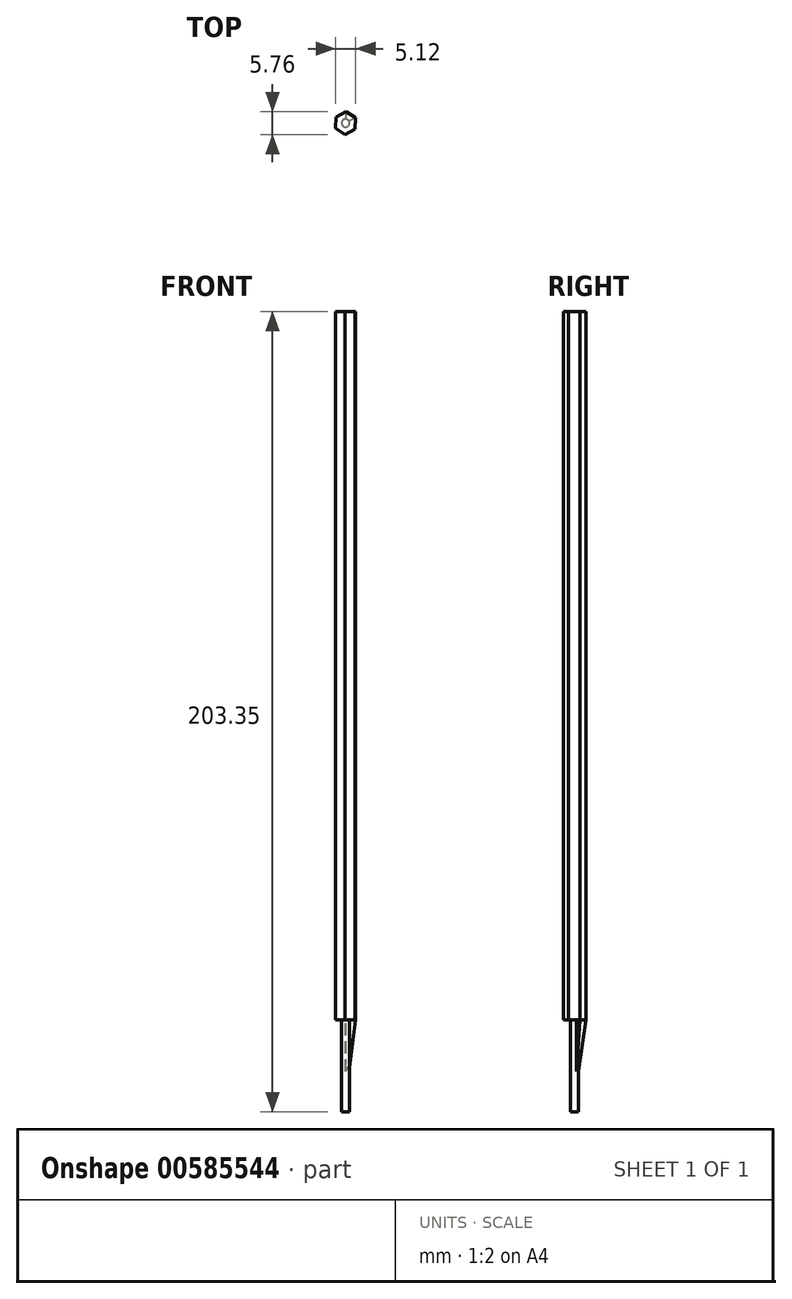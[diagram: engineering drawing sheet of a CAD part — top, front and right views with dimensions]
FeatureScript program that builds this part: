
annotation { "Feature Type Name" : "Feature", "Feature Type Description" : "" }
export const myFeature = defineFeature(function(context is Context, id is Id, definition is map)
    precondition{}
    {
        {
            var Q0;
            Q0=qCreatedBy(makeId("Top.planeOp"),FACE);
            var sketch = newSketch(context, id + "F0", { "sketchPlane" : qUnion([Q0])});
            skCircle(sketch, "E0", {"center": v(0, 0) * mm, "radius": 2.5 * mm});
            skCircle(sketch, "E1.cCircle", {"center": v(0, 0) * mm, "radius": 2.5 * mm, "construction": true});
            skLineSegment(sketch, "E1.0", {"start": v(0.12, 2.88) * mm, "end": v(2.56, 1.34) * mm});
            skLineSegment(sketch, "E1.1", {"start": v(2.56, 1.34) * mm, "end": v(2.44, -1.54) * mm});
            skLineSegment(sketch, "E1.2", {"start": v(2.44, -1.54) * mm, "end": v(-0.12, -2.88) * mm});
            skLineSegment(sketch, "E1.3", {"start": v(-0.12, -2.88) * mm, "end": v(-2.56, -1.34) * mm});
            skLineSegment(sketch, "E1.4", {"start": v(-2.56, -1.34) * mm, "end": v(-2.44, 1.54) * mm});
            skLineSegment(sketch, "E1.5", {"start": v(-2.44, 1.54) * mm, "end": v(0.12, 2.88) * mm});
            skPoint(sketch, "E1.0.midPoint", {"position": v(1.34, 2.11) * mm});
            skCircle(sketch, "E2", {"center": v(0, 0) * mm, "radius": 1 * mm});
            skSolve(sketch);
        }
        {
            var Q0;
            {var subQ0=sQuery(id+"F0.wireOp",EDGE,"E1.4");var subQ1=sQuery(id+"F0.wireOp",EDGE,"E0");var subQ2=makeQuery(id+"F0.imprint","INTERSECT",VERTEX,{"derivedFrom":[subQ1,subQ0]});Q0=makeQuery(id+"F0.imprint","IMPRINT",FACE,{"disambiguationData":[TD([[makeQuery(id+"F0.imprint","IMPRINT",EDGE,{"disambiguationData":[TD([[subQ2,-1.0]])],"derivedFrom":subQ1}),-1.0]])]});}
            var Q1;
            {var subQ0=sQuery(id+"F0.wireOp",EDGE,"E1.3");var subQ1=sQuery(id+"F0.wireOp",EDGE,"E0");var subQ2=makeQuery(id+"F0.imprint","INTERSECT",VERTEX,{"derivedFrom":[subQ1,subQ0]});Q1=makeQuery(id+"F0.imprint","IMPRINT",FACE,{"disambiguationData":[TD([[makeQuery(id+"F0.imprint","IMPRINT",EDGE,{"disambiguationData":[TD([[subQ2,-1.0]])],"derivedFrom":subQ1}),-1.0]])]});}
            var Q2;
            {var subQ0=sQuery(id+"F0.wireOp",EDGE,"E1.5");var subQ1=sQuery(id+"F0.wireOp",EDGE,"E0");var subQ2=makeQuery(id+"F0.imprint","INTERSECT",VERTEX,{"derivedFrom":[subQ1,subQ0]});Q2=makeQuery(id+"F0.imprint","IMPRINT",FACE,{"disambiguationData":[TD([[makeQuery(id+"F0.imprint","IMPRINT",EDGE,{"disambiguationData":[TD([[subQ2,1.0]])],"derivedFrom":subQ1}),-1.0]])]});}
            var Q3;
            {var subQ0=sQuery(id+"F0.wireOp",EDGE,"E1.5");var subQ1=sQuery(id+"F0.wireOp",EDGE,"E0");var subQ2=makeQuery(id+"F0.imprint","INTERSECT",VERTEX,{"derivedFrom":[subQ1,subQ0]});Q3=makeQuery(id+"F0.imprint","IMPRINT",FACE,{"disambiguationData":[TD([[makeQuery(id+"F0.imprint","IMPRINT",EDGE,{"disambiguationData":[TD([[subQ2,-1.0]])],"derivedFrom":subQ1}),-1.0]])]});}
            var Q4;
            {var subQ0=sQuery(id+"F0.wireOp",EDGE,"E1.2");var subQ1=sQuery(id+"F0.wireOp",EDGE,"E0");var subQ2=makeQuery(id+"F0.imprint","INTERSECT",VERTEX,{"derivedFrom":[subQ1,subQ0]});Q4=makeQuery(id+"F0.imprint","IMPRINT",FACE,{"disambiguationData":[TD([[makeQuery(id+"F0.imprint","IMPRINT",EDGE,{"disambiguationData":[TD([[subQ2,-1.0]])],"derivedFrom":subQ1}),-1.0]])]});}
            var Q5;
            {var subQ0=sQuery(id+"F0.wireOp",EDGE,"E1.0");var subQ1=sQuery(id+"F0.wireOp",EDGE,"E0");var subQ2=makeQuery(id+"F0.imprint","INTERSECT",VERTEX,{"derivedFrom":[subQ1,subQ0]});Q5=makeQuery(id+"F0.imprint","IMPRINT",FACE,{"disambiguationData":[TD([[makeQuery(id+"F0.imprint","IMPRINT",EDGE,{"disambiguationData":[TD([[subQ2,1.0]])],"derivedFrom":subQ1}),-1.0]])]});}
            var Q6;
            Q6=makeQuery(id+"F0.imprint","IMPRINT",FACE,{"disambiguationData":[TD([[makeQuery(id+"F0.imprint","IMPRINT",EDGE,{"derivedFrom":sQuery(id+"F0.wireOp",EDGE,"E2")}),-1.0]])]});
            extrude(context, id + "F1", {"entities" : qUnion([Q0, Q1, Q2, Q3, Q4, Q5, Q6]), "oppositeDirection" : true, "depth" : 180 * mm, "offsetDistance" : 25.4 * mm});
        }
        {
            var Q0;
            Q0=makeQuery(id+"F0.imprint","IMPRINT",FACE,{"disambiguationData":[TD([[makeQuery(id+"F0.imprint","IMPRINT",EDGE,{"derivedFrom":sQuery(id+"F0.wireOp",EDGE,"E2")}),1.0]])]});
            extrude(context, id + "F2", {"entities" : qUnion([Q0]), "operationType" : NewBodyOperationType.ADD, "oppositeDirection" : true, "depth" : 203.35 * mm, "offsetDistance" : 25.4 * mm});
        }
        {
            var Q0;
            Q0=qCreatedBy(makeId("Top.planeOp"),FACE);
            cPlane(context, id + "F3", {"entities" : qUnion([Q0]), "cplaneType" : CPlaneType.OFFSET, "offset" : 200 * mm, "oppositeDirection" : true, "width" : 152.4 * mm, "height" : 152.4 * mm});
        }
        {
            var Q0;
            Q0=qCreatedBy(id+"F3.planeOp",FACE);
            var sketch = newSketch(context, id + "F4", { "sketchPlane" : qUnion([Q0])});
            skCircle(sketch, "E3", {"center": v(0, 0) * mm, "radius": 0.25 * mm});
            skSolve(sketch);
        }
        {
            var Q1;
            Q1=sQuery(id+"F4.wireOp",VERTEX,"E3.center");
            var Q2;
            Q2=makeQuery(id+"F1.opExtrude","SWEPT_FACE",FACE,{"disambiguationData":[OSD([sQuery(id+"F0.wireOp",EDGE,"E1.0")])]});
            loft(context, id + "F5", {"operationType" : NewBodyOperationType.ADD, "sheetProfilesArray" : [{ "sheetProfileEntities" : qUnion([Q1]) }, { "sheetProfileEntities" : qUnion([Q2]) }]});
        }
    });
